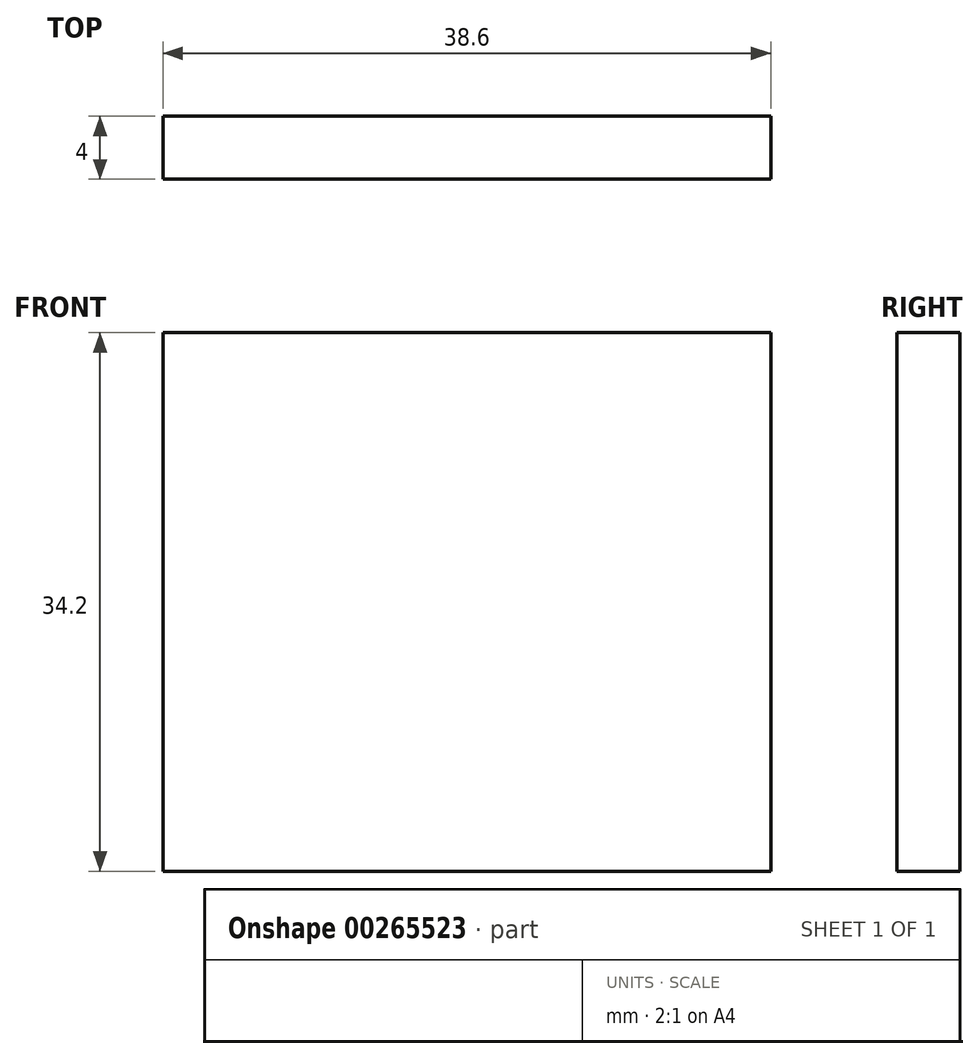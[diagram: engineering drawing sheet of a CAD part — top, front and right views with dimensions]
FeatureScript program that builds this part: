
annotation { "Feature Type Name" : "Feature", "Feature Type Description" : "" }
export const myFeature = defineFeature(function(context is Context, id is Id, definition is map)
    precondition{}
    {
        {
            var Q0;
            Q0=qCreatedBy(makeId("Front.planeOp"),FACE);
            var sketch = newSketch(context, id + "F0", { "sketchPlane" : qUnion([Q0])});
            skLineSegment(sketch, "E0.bottom", {"start": v(-19.3, -17.1) * mm, "end": v(19.3, -17.1) * mm});
            skLineSegment(sketch, "E0.top", {"start": v(-19.3, 17.1) * mm, "end": v(19.3, 17.1) * mm});
            skLineSegment(sketch, "E0.left", {"start": v(-19.3, -17.1) * mm, "end": v(-19.3, 17.1) * mm});
            skLineSegment(sketch, "E0.right", {"start": v(19.3, -17.1) * mm, "end": v(19.3, 17.1) * mm});
            skPoint(sketch, "E0.middle", {"position": v(0, 0) * mm});
            skSolve(sketch);
        }
        {
            var Q0;
            Q0=makeQuery(id+"F0.imprint","IMPRINT",FACE,{"disambiguationData":[TD([[makeQuery(id+"F0.imprint","IMPRINT",EDGE,{"derivedFrom":sQuery(id+"F0.wireOp",EDGE,"E0.bottom")}),1.0]])]});
            extrude(context, id + "F1", {"entities" : qUnion([Q0]), "depth" : 4 * mm});
        }
    });
